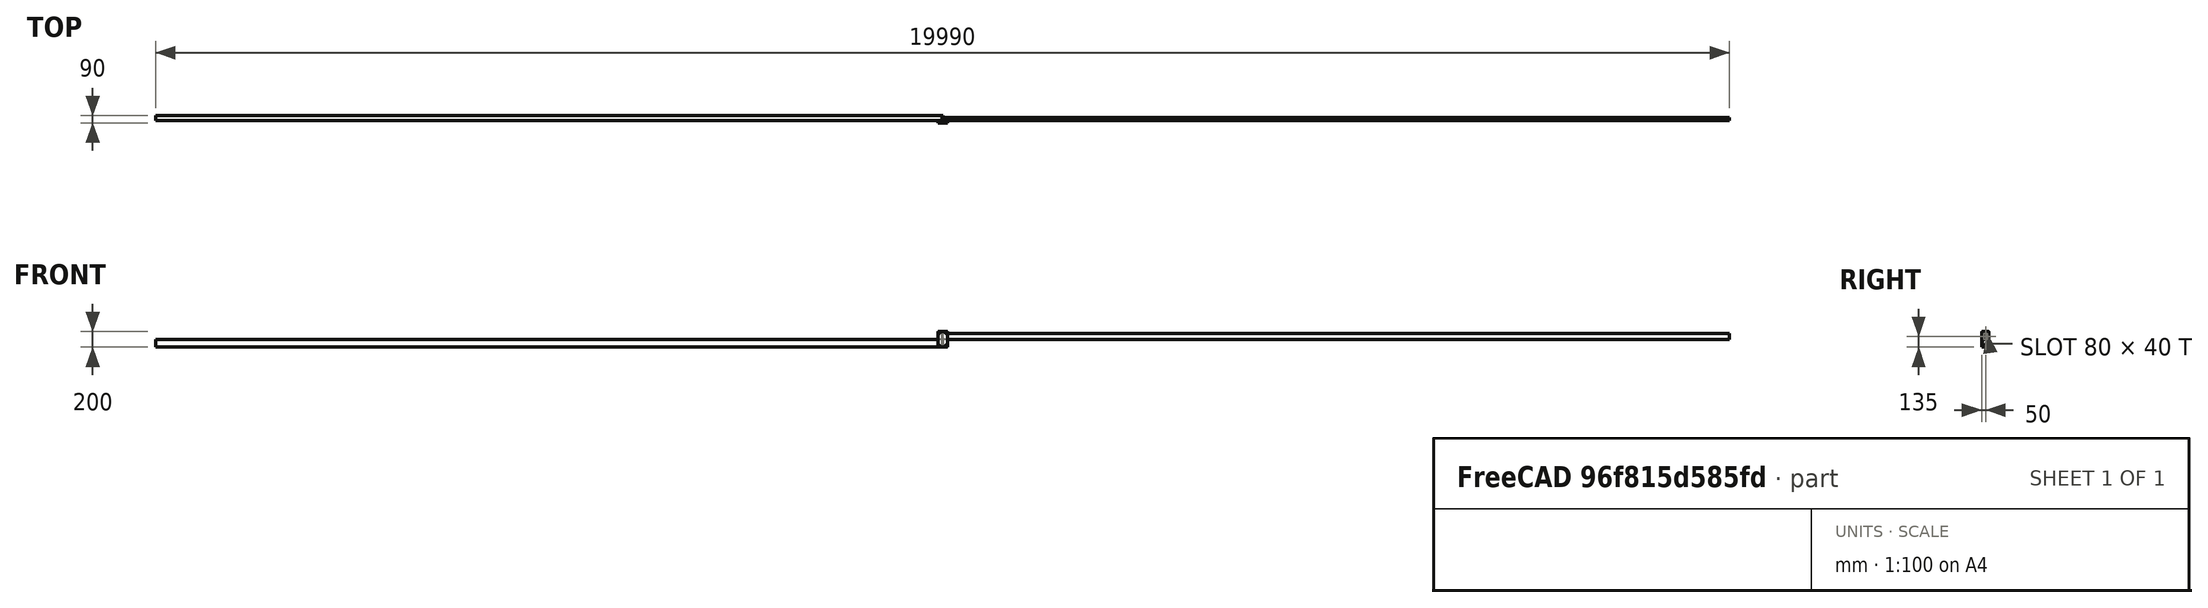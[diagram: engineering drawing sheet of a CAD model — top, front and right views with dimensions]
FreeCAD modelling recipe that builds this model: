
FCSTD DOCUMENT  (FreeCAD 0.16RUnknown)
Label: part
License: All rights reserved
LicenseURL: http://en.wikipedia.org/wiki/All_rights_reserved
objects: Sketcher::SketchObject×4, PartDesign::Pocket×3, PartDesign::Fillet×2, PartDesign::Pad×1, Fem::FemSolverObjectPython×1, Fem::FemMeshObject×1, Fem::ConstraintFixed×1, Fem::ConstraintForce×1, App::MaterialObjectPython×1, Fem::FemAnalysisPython×1
note: 14 computed .brp shape members not serialized (recipe doc carries the construction recipe); baked Part::Feature solids carry a one-line shape summary decoded from their .brp

FEATURE [Sketcher::SketchObject] Sketch
  sketch-geometry (8):
    g0: LineSegment StartX=60 StartY=0 StartZ=0 EndX=60 EndY=-10 EndZ=0
    g1: LineSegment StartX=60 StartY=-10 StartZ=0 EndX=-60 EndY=-10 EndZ=0
    g2: LineSegment StartX=-60 StartY=-10 StartZ=0 EndX=-60 EndY=0 EndZ=0
    g3: LineSegment StartX=-60 StartY=0 StartZ=0 EndX=-5 EndY=0 EndZ=0
    g4: LineSegment StartX=-5 StartY=0 StartZ=0 EndX=-5 EndY=80 EndZ=0
    g5: LineSegment StartX=-5 StartY=80 StartZ=0 EndX=5 EndY=80 EndZ=0
    g6: LineSegment StartX=5 StartY=80 StartZ=0 EndX=5 EndY=0 EndZ=0
    g7: LineSegment StartX=5 StartY=0 StartZ=0 EndX=60 EndY=0 EndZ=0
  constraints (24):
    c: PointOnObject(g0,g-1)
    c: Vertical(g0)
    c: Coincident(g0,g1)
    c: Coincident(g1,g2)
    c: PointOnObject(g2,g-1)
    c: Vertical(g2)
    c: Coincident(g2,g3)
    c: PointOnObject(g3,g-1)
    c: Coincident(g3,g4)
    c: Vertical(g4)
    c: Coincident(g4,g5)
    c: Horizontal(g5)
    c: Coincident(g5,g6)
    c: PointOnObject(g6,g-1)
    c: Vertical(g6)
    c: Coincident(g6,g7)
    c: Equal(g2,g0)
    c: Equal(g0,g5)
    c: Equal(g7,g3)
    c: Symmetric(g0,g1,g-2)
    c: DistanceY(g2,g2) = 10
    c: Coincident(g0,g7)
    c: DistanceX(g3,g3) = 55
    c: DistanceY(g4,g4) = 80
FEATURE [PartDesign::Pad] Pad
  Length = 200
  Length2 = 100
  Sketch = -> Sketch
  Type = 0
FEATURE [Sketcher::SketchObject] Sketch001
  ExternalGeometry = -> [Pad]
  Placement = pos=(5,0,0) rot=(0.57735,0.57735,0.57735;2.0944rad)
  Support = -> Pad [Face7]
  sketch-geometry (3):
    g0: LineSegment StartX=20 StartY=0 StartZ=0 EndX=80 EndY=0 EndZ=0
    g1: LineSegment StartX=80 StartY=0 StartZ=0 EndX=80 EndY=100 EndZ=0
    g2: LineSegment StartX=80 StartY=100 StartZ=0 EndX=20 EndY=0 EndZ=0
  constraints (8):
    c: Coincident(g0,g-3)
    c: Horizontal(g0)
    c: Coincident(g0,g1)
    c: PointOnObject(g1,g-3)
    c: Coincident(g1,g2)
    c: Coincident(g2,g0)
    c: DistanceX(g-1,g0) = 20
    c: DistanceY(g1,g1) = 100
FEATURE [PartDesign::Pocket] Pocket
  Length = 5
  Sketch = -> Sketch001
  Type = 1
FEATURE [Sketcher::SketchObject] Sketch002
  ExternalGeometry = -> [Pocket]
  Placement = pos=(-5,0,0) rot=(0.57735,-0.57735,-0.57735;2.0944rad)
  Support = -> Pocket [Face9]
  sketch-geometry (4):
    g0: ArcOfCircle CenterX=-40 CenterY=155 CenterZ=0 NormalX=0 NormalY=0 NormalZ=1 Radius=20 StartAngle=0 EndAngle=3.14159
    g1: ArcOfCircle CenterX=-40 CenterY=115 CenterZ=0 NormalX=0 NormalY=0 NormalZ=1 Radius=20 StartAngle=3.14159 EndAngle=6.28319
    g2: LineSegment StartX=-60 StartY=155 StartZ=0 EndX=-60 EndY=115 EndZ=0
    g3: LineSegment StartX=-20 StartY=155 StartZ=0 EndX=-20 EndY=115 EndZ=0
  constraints (10):
    c: Tangent(g0,g3) = 1.5708
    c: Tangent(g0,g2) = -1.5708
    c: Tangent(g2,g1) = -1.5708
    c: Tangent(g3,g1) = 1.5708
    c: Vertical(g2)
    c: Equal(g0,g1)
    c: Radius(g0) = 20
    c: DistanceX(g0,g-1) = 40
    c: DistanceY(g2,g2) = 40
    c: DistanceY(g0,g-3) = 45
FEATURE [PartDesign::Pocket] Pocket001
  Length = 5
  Sketch = -> Sketch002
  Type = 1
FEATURE [Sketcher::SketchObject] Sketch003
  Placement = pos=(0,-10,0) rot=(1,0,0;1.5708rad)
  Support = -> Pocket001 [Face3]
  sketch-geometry (7):
    g0: Circle CenterX=-40 CenterY=180 CenterZ=0 NormalX=0 NormalY=0 NormalZ=1 Radius=6
    g1: Circle CenterX=40 CenterY=180 CenterZ=0 NormalX=0 NormalY=0 NormalZ=1 Radius=6
    g2: LineSegment [constr] StartX=-40 StartY=180 StartZ=0 EndX=40 EndY=180 EndZ=0
    g3: Circle CenterX=-40 CenterY=20 CenterZ=0 NormalX=0 NormalY=0 NormalZ=1 Radius=6
    g4: LineSegment [constr] StartX=-40 StartY=180 StartZ=0 EndX=-40 EndY=20 EndZ=0
    g5: Circle CenterX=40 CenterY=20 CenterZ=0 NormalX=0 NormalY=0 NormalZ=1 Radius=6
    g6: LineSegment [constr] StartX=-40 StartY=20 StartZ=0 EndX=40 EndY=20 EndZ=0
  constraints (18):
    c: Radius(g0) = 6
    c: Equal(g0,g1) = 6
    c: Coincident(g0,g2)
    c: Coincident(g1,g2)
    c: Distance(g2) = 80
    c: Angle(g2) = 0
    c: Equal(g0,g3) = 6
    c: Coincident(g0,g4)
    c: Coincident(g3,g4)
    c: Distance(g4) = 160
    c: Perpendicular(g4,g2)
    c: Equal(g0,g5) = 6
    c: Coincident(g3,g6)
    c: Coincident(g5,g6)
    c: Equal(g2,g6)
    c: Parallel(g6,g2)
    c: DistanceY(g-1,g3) = 20
    c: Symmetric(g1,g0,g-2)
FEATURE [PartDesign::Pocket] Pocket002
  Length = 5
  Sketch = -> Sketch003
  Type = 1
FEATURE [PartDesign::Fillet] Fillet
  Base = -> Pocket002 [Edge5,Edge42]
  Radius = 10
FEATURE [PartDesign::Fillet] Fillet001
  Base = -> Fillet [Edge22,Edge19,Edge8,Edge12,Edge11,Edge25]
  Radius = 10
FEATURE [Fem::FemSolverObjectPython] CalculiX  # FEM object (typed FeaturePython)
  AnalysisType = 0
  EigenmodeHighLimit = 1000000
  EigenmodeLowLimit = 0
  NumberOfEigenmodes = 10
  SolverType = FemSolverCalculix
FEATURE [Fem::FemMeshObject] gmsh2cad
FEATURE [Fem::ConstraintFixed] FemConstraintFixed
  NormalDirection = (1,0,0)
  Normals = (48) [(-1,0,0),(0.5,-1.92296e-16,-0.866025),(0.5,1.92296e-16,0.866025),(-1,-7.34476e-31,-3.30778e-15),(-1,0,0),(0.5,-1.92296e-16,-0.866025),+42 more]
  Points = (48) [(-34,0,180),(-43,1.77636e-15,185.196),(-43,-1.77636e-15,174.804),(-34,0,180),(-34,-5,180),(-43,-5,185.196),(-43,-5,174.804),(-34,-5,180),+40 more]
  References = -> [Fillet001]
  Scale = 3
FEATURE [Fem::ConstraintForce] FemConstraintForce
  DirectionVector = (0,1,0)
  Force = 5000
  NormalDirection = (0,-1,0)
  Points = (12) [(5,60,155),(5,60,141.667),(5,60,128.333),(5,60,115),(0,60,155),(0,60,141.667),(0,60,128.333),(0,60,115),(-5,60,155),(-5,60,141.667),(-5,60,128.333),+1 more]
  References = -> [Fillet001]
  Reversed = true
  Scale = 3
FEATURE [App::MaterialObjectPython] MechanicalMaterial  # material (typed FeaturePython)
  Material = Density=7900 kg/m^3; Description=Standard steel material for CalculiX sample calculations; Father=Metal; Name=CalculiX-Steel; PoissonRatio=0.3; YoungsModulus=210000 MPa
FEATURE [Fem::FemAnalysisPython] MechanicalAnalysis  # FEM object (typed FeaturePython)
  Member = -> [CalculiX,gmsh2cad,FemConstraintFixed,FemConstraintForce,MechanicalMaterial]
